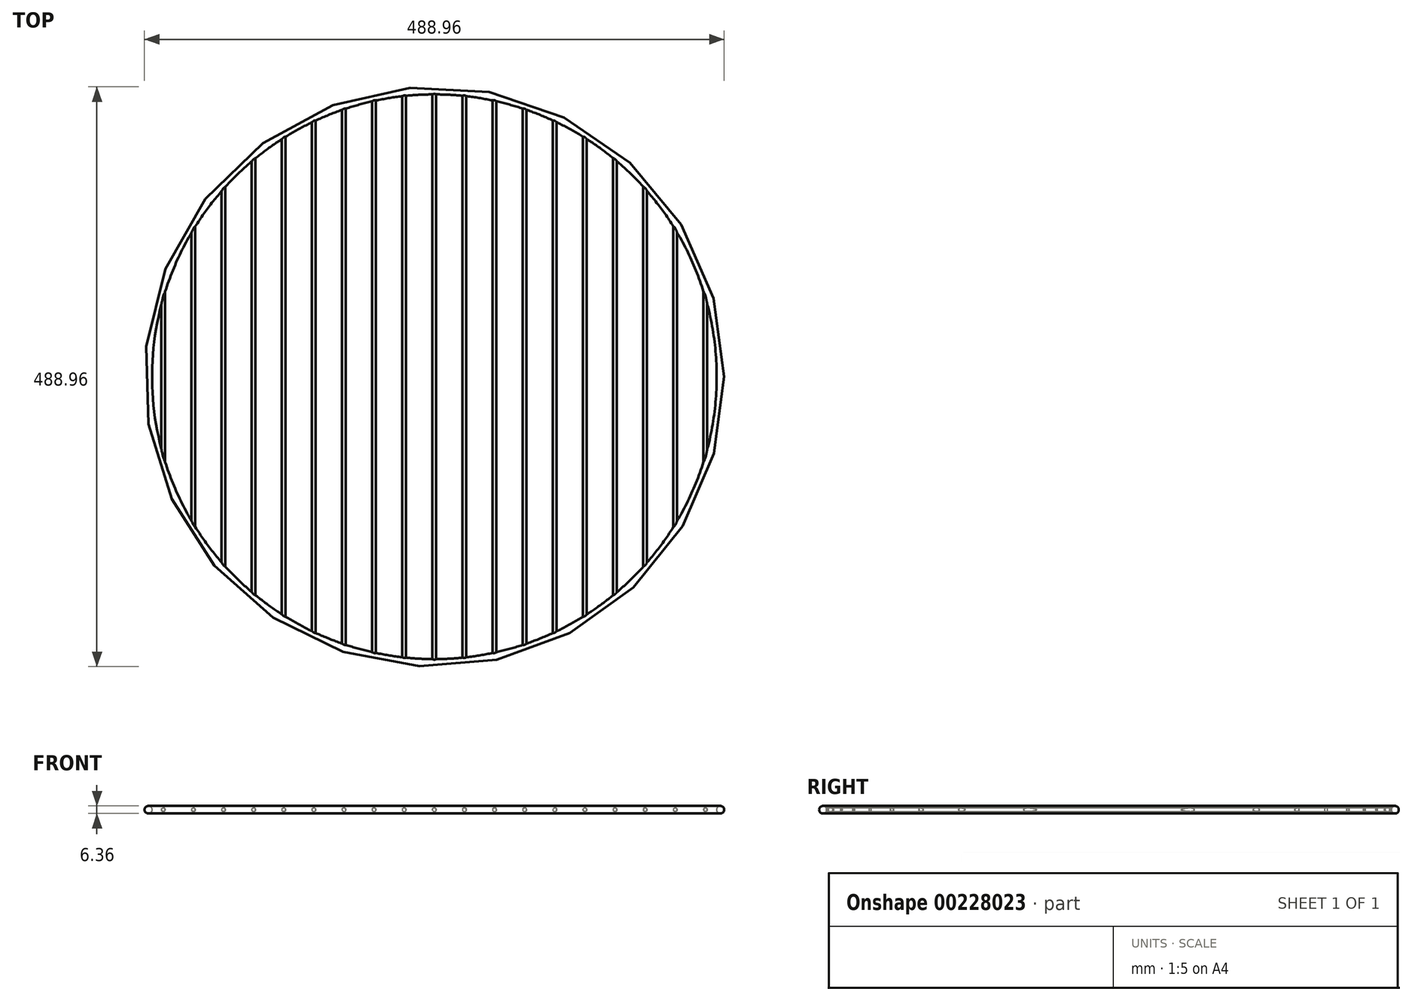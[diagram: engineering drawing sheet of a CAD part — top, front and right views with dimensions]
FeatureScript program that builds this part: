
annotation { "Feature Type Name" : "Feature", "Feature Type Description" : "" }
export const myFeature = defineFeature(function(context is Context, id is Id, definition is map)
    precondition{}
    {
        {
            var Q0;
            Q0=qCreatedBy(makeId("Front.planeOp"),FACE);
            var sketch = newSketch(context, id + "F0", { "sketchPlane" : qUnion([Q0])});
            skCircle(sketch, "E0", {"center": v(241.3, 0) * mm, "radius": 3.17 * mm});
            skLineSegment(sketch, "E1", {"start": v(0, 0) * mm, "end": v(0, 24.34) * mm, "construction": true});
            skSolve(sketch);
        }
        {
            var Q0;
            Q0=makeQuery(id+"F0.imprint","IMPRINT",FACE,{"disambiguationData":[TD([[makeQuery(id+"F0.imprint","IMPRINT",EDGE,{"derivedFrom":sQuery(id+"F0.wireOp",EDGE,"E0")}),1.0]])]});
            var Q1;
            Q1=sQuery(id+"F0.wireOp",EDGE,"E0");
            var Q2;
            Q2=sQuery(id+"F0.wireOp",EDGE,"E1");
            revolve(context, id + "F1", {"entities" : qUnion([Q0]), "surfaceEntities" : qUnion([Q1]), "axis" : qUnion([Q2]), "revolveType" : RevolveType.FULL});
        }
        {
            var Q0;
            Q0=qCreatedBy(makeId("Front.planeOp"),FACE);
            var sketch = newSketch(context, id + "F2", { "sketchPlane" : qUnion([Q0])});
            skCircle(sketch, "E2", {"center": v(0, 0) * mm, "radius": 1.59 * mm});
            skCircle(sketch, "E3.1.0.0", {"center": v(25.4, 0) * mm, "radius": 1.59 * mm});
            skCircle(sketch, "E3.2.0.0", {"center": v(50.8, 0) * mm, "radius": 1.59 * mm});
            skCircle(sketch, "E3.3.0.0", {"center": v(76.2, 0) * mm, "radius": 1.59 * mm});
            skCircle(sketch, "E3.4.0.0", {"center": v(101.6, 0) * mm, "radius": 1.59 * mm});
            skCircle(sketch, "E3.5.0.0", {"center": v(127, 0) * mm, "radius": 1.59 * mm});
            skCircle(sketch, "E3.6.0.0", {"center": v(152.4, 0) * mm, "radius": 1.59 * mm});
            skCircle(sketch, "E3.7.0.0", {"center": v(177.8, 0) * mm, "radius": 1.59 * mm});
            skCircle(sketch, "E3.8.0.0", {"center": v(203.2, 0) * mm, "radius": 1.59 * mm});
            skCircle(sketch, "E3.9.0.0", {"center": v(228.6, 0) * mm, "radius": 1.59 * mm});
            skLineSegment(sketch, "E3.direction1", {"start": v(0, 0) * mm, "end": v(25.4, 0) * mm, "construction": true});
            skCircle(sketch, "E4.1.0.0", {"center": v(-25.4, 0) * mm, "radius": 1.59 * mm});
            skCircle(sketch, "E4.2.0.0", {"center": v(-50.8, 0) * mm, "radius": 1.59 * mm});
            skCircle(sketch, "E4.3.0.0", {"center": v(-76.2, 0) * mm, "radius": 1.59 * mm});
            skCircle(sketch, "E4.4.0.0", {"center": v(-101.6, 0) * mm, "radius": 1.59 * mm});
            skCircle(sketch, "E4.5.0.0", {"center": v(-127, 0) * mm, "radius": 1.59 * mm});
            skCircle(sketch, "E4.6.0.0", {"center": v(-152.4, 0) * mm, "radius": 1.59 * mm});
            skCircle(sketch, "E4.7.0.0", {"center": v(-177.8, 0) * mm, "radius": 1.59 * mm});
            skCircle(sketch, "E4.8.0.0", {"center": v(-203.2, 0) * mm, "radius": 1.59 * mm});
            skCircle(sketch, "E4.9.0.0", {"center": v(-228.6, 0) * mm, "radius": 1.59 * mm});
            skLineSegment(sketch, "E4.direction1", {"start": v(0, 0) * mm, "end": v(-25.4, 0) * mm, "construction": true});
            skSolve(sketch);
        }
        {
            var Q0;
            Q0 = qSketchRegion(id + "F2", true);
            extrude(context, id + "F3", {"entities" : qUnion([Q0]), "operationType" : NewBodyOperationType.ADD, "endBound" : BoundingType.UP_TO_NEXT, "depth" : 25.4 * mm, "hasSecondDirection" : true, "secondDirectionBound" : SecondDirectionBoundingType.UP_TO_NEXT, "secondDirectionOppositeDirection" : true, "secondDirectionDepth" : 25.4 * mm});
        }
    });
